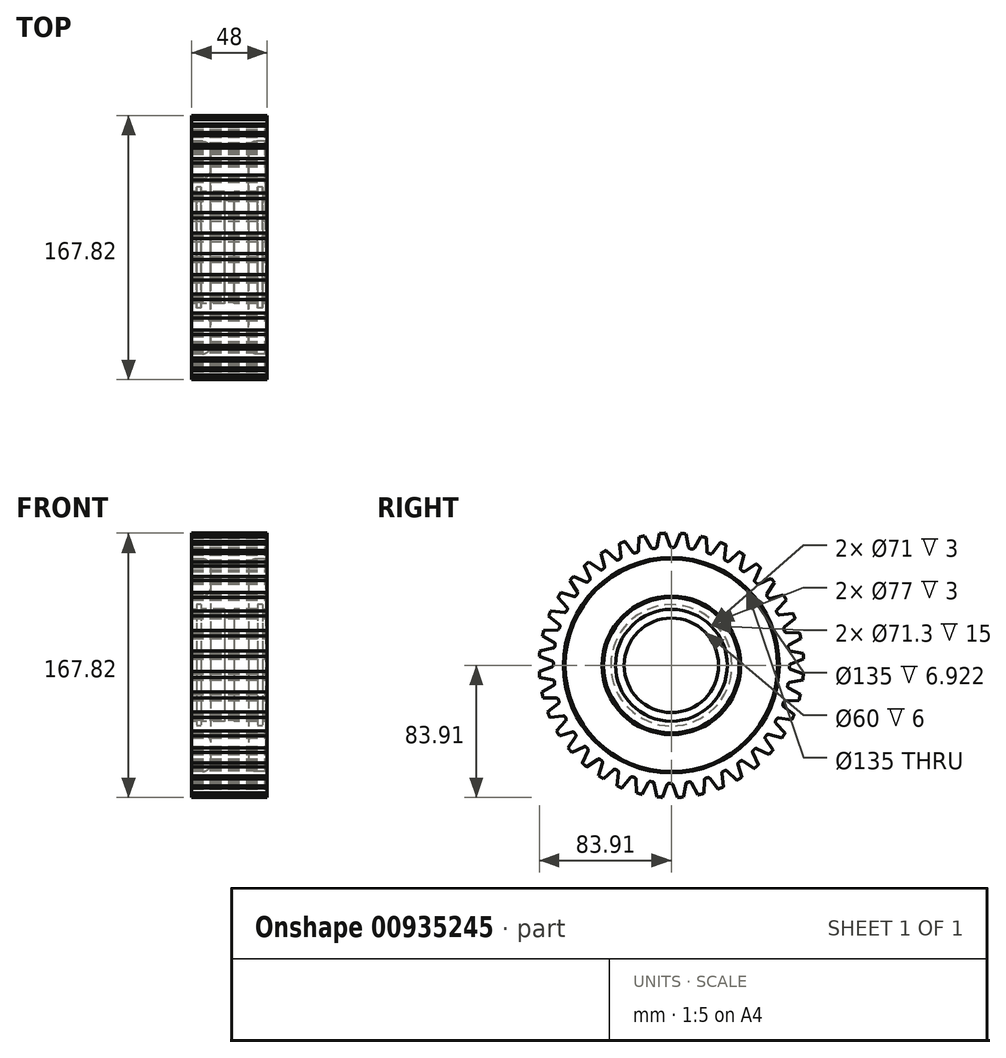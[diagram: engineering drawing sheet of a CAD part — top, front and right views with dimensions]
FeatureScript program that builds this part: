
annotation { "Feature Type Name" : "Feature", "Feature Type Description" : "" }
export const myFeature = defineFeature(function(context is Context, id is Id, definition is map)
    precondition{}
    {
        {
            var Q0;
            Q0=qCreatedBy(makeId("Front.planeOp"),FACE);
            var sketch = newSketch(context, id + "F0", { "sketchPlane" : qUnion([Q0])});
            skLineSegment(sketch, "E0", {"start": v(0, 84) * mm, "end": v(-24, 84) * mm});
            skLineSegment(sketch, "E1", {"start": v(-24, 84) * mm, "end": v(-24, 67.5) * mm});
            skLineSegment(sketch, "E2", {"start": v(-24, 0) * mm, "end": v(0, 0) * mm});
            skLineSegment(sketch, "E3", {"start": v(-24, 35.5) * mm, "end": v(-21, 35.5) * mm});
            skLineSegment(sketch, "E4", {"start": v(-21, 35.5) * mm, "end": v(-21, 38.5) * mm});
            skLineSegment(sketch, "E5", {"start": v(-21, 38.5) * mm, "end": v(-18, 38.5) * mm});
            skLineSegment(sketch, "E6", {"start": v(-18, 38.5) * mm, "end": v(-18, 35.65) * mm});
            skLineSegment(sketch, "E7", {"start": v(-18, 35.65) * mm, "end": v(-3, 35.65) * mm});
            skLineSegment(sketch, "E8", {"start": v(-3, 35.65) * mm, "end": v(-3, 30) * mm});
            skLineSegment(sketch, "E9", {"start": v(-3, 30) * mm, "end": v(0, 30) * mm});
            skLineSegment(sketch, "E10", {"start": v(-24, 44) * mm, "end": v(-17.08, 44) * mm});
            skLineSegment(sketch, "E11", {"start": v(-12, 49.08) * mm, "end": v(-12, 62.42) * mm});
            skLineSegment(sketch, "E12", {"start": v(-17.08, 67.5) * mm, "end": v(-24, 67.5) * mm});
            skPoint(sketch, "E13.visualSharp", {"position": v(-12, 67.5) * mm});
            skArc(sketch, "E13.filletArc", {"start": v(-12, 62.42) * mm, "mid": v(-13.49, 66.01) * mm, "end": v(-17.08, 67.5) * mm});
            skPoint(sketch, "E14.visualSharp", {"position": v(-12, 44) * mm});
            skArc(sketch, "E14.filletArc", {"start": v(-17.08, 44) * mm, "mid": v(-13.49, 45.49) * mm, "end": v(-12, 49.08) * mm});
            skLineSegment(sketch, "E15.trimOffspring", {"start": v(-24, 44) * mm, "end": v(-24, 35.5) * mm});
            skLineSegment(sketch, "E16.MirrorCS", {"start": v(0, 84) * mm, "end": v(24, 84) * mm});
            skLineSegment(sketch, "E17.MirrorCS", {"start": v(24, 84) * mm, "end": v(24, 67.5) * mm});
            skLineSegment(sketch, "E18.MirrorCS", {"start": v(17.08, 67.5) * mm, "end": v(24, 67.5) * mm});
            skArc(sketch, "E19.MirrorCS", {"start": v(12, 62.42) * mm, "mid": v(13.49, 66.01) * mm, "end": v(17.08, 67.5) * mm});
            skLineSegment(sketch, "E20.MirrorCS", {"start": v(12, 49.08) * mm, "end": v(12, 62.42) * mm});
            skArc(sketch, "E21.MirrorCS", {"start": v(17.08, 44) * mm, "mid": v(13.49, 45.49) * mm, "end": v(12, 49.08) * mm});
            skLineSegment(sketch, "E22.MirrorCS", {"start": v(24, 44) * mm, "end": v(17.08, 44) * mm});
            skLineSegment(sketch, "E23.MirrorCS", {"start": v(24, 44) * mm, "end": v(24, 35.5) * mm});
            skLineSegment(sketch, "E24.MirrorCS", {"start": v(24, 35.5) * mm, "end": v(21, 35.5) * mm});
            skLineSegment(sketch, "E25.MirrorCS", {"start": v(21, 38.5) * mm, "end": v(18, 38.5) * mm});
            skLineSegment(sketch, "E26.MirrorCS", {"start": v(21, 35.5) * mm, "end": v(21, 38.5) * mm});
            skLineSegment(sketch, "E27.MirrorCS", {"start": v(18, 38.5) * mm, "end": v(18, 35.65) * mm});
            skLineSegment(sketch, "E28.MirrorCS", {"start": v(18, 35.65) * mm, "end": v(3, 35.65) * mm});
            skLineSegment(sketch, "E29.MirrorCS", {"start": v(3, 35.65) * mm, "end": v(3, 30) * mm});
            skLineSegment(sketch, "E30.MirrorCS", {"start": v(3, 30) * mm, "end": v(0, 30) * mm});
            skSolve(sketch);
        }
        {
            var Q0;
            Q0=makeQuery(id+"F0.imprint","IMPRINT",FACE,{"disambiguationData":[TD([[makeQuery(id+"F0.imprint","IMPRINT",EDGE,{"derivedFrom":sQuery(id+"F0.wireOp",EDGE,"E0")}),1.0]])]});
            var Q1;
            Q1=sQuery(id+"F0.wireOp",EDGE,"E2");
            revolve(context, id + "F1", {"surfaceOperationType" : NewSurfaceOperationType.NEW, "entities" : qUnion([Q0]), "axis" : qUnion([Q1]), "revolveType" : RevolveType.FULL});
        }
        {
            var Q0;
            Q0=qCreatedBy(makeId("Right.planeOp"),FACE);
            var sketch = newSketch(context, id + "F2", { "sketchPlane" : qUnion([Q0])});
            skArc(sketch, "E31", {"start": v(1.48, 74.99) * mm, "mid": v(0.85, 75) * mm, "end": v(0.23, 75) * mm});
            skArc(sketch, "E32.0.0", {"start": v(5.6, 83.81) * mm, "mid": v(0.85, 84) * mm, "end": v(-3.9, 83.9) * mm});
            skLineSegment(sketch, "E33", {"start": v(2.7, 75.82) * mm, "end": v(5.6, 83.81) * mm});
            skLineSegment(sketch, "E34.MirrorCS", {"start": v(-0.96, 75.84) * mm, "end": v(-3.9, 83.9) * mm});
            skPoint(sketch, "E35.trimOffspring.end.orphan", {"position": v(-0.9, 84.76) * mm});
            skPoint(sketch, "E36.visualSharp", {"position": v(-0.66, 75) * mm});
            skArc(sketch, "E36.filletArc", {"start": v(-0.96, 75.84) * mm, "mid": v(-0.5, 75.23) * mm, "end": v(0.23, 75) * mm});
            skPoint(sketch, "E37.visualSharp", {"position": v(2.38, 74.96) * mm});
            skArc(sketch, "E37.filletArc", {"start": v(1.48, 74.99) * mm, "mid": v(2.22, 75.2) * mm, "end": v(2.7, 75.82) * mm});
            skSolve(sketch);
        }
        {
            var Q0;
            Q0=makeQuery(id+"F2.imprint","IMPRINT",FACE,{"disambiguationData":[TD([[makeQuery(id+"F2.imprint","IMPRINT",EDGE,{"derivedFrom":sQuery(id+"F2.wireOp",EDGE,"E31")}),-1.0]])]});
            extrude(context, id + "F3", {"entities" : qUnion([Q0]), "operationType" : NewBodyOperationType.REMOVE, "oppositeDirection" : true, "depth" : 50.8 * mm, "offsetDistance" : 25.4 * mm, "symmetric" : true});
        }
        {
            var Q0;
            Q0=makeQuery(id+"F3.boolean.opBoolean","COPY",FACE,{"derivedFrom":makeQuery(id+"F3.opExtrude","SWEPT_FACE",FACE,{"disambiguationData":[OSD([sQuery(id+"F2.wireOp",EDGE,"E34.MirrorCS")])]})});
            var Q1;
            Q1=makeQuery(id+"F3.boolean.opBoolean","COPY",FACE,{"derivedFrom":makeQuery(id+"F3.opExtrude","SWEPT_FACE",FACE,{"disambiguationData":[OSD([sQuery(id+"F2.wireOp",EDGE,"E36.filletArc")])]})});
            var Q2;
            Q2=makeQuery(id+"F3.boolean.opBoolean","COPY",FACE,{"derivedFrom":makeQuery(id+"F3.opExtrude","SWEPT_FACE",FACE,{"disambiguationData":[OSD([sQuery(id+"F2.wireOp",EDGE,"E31")])]})});
            var Q3;
            Q3=makeQuery(id+"F3.boolean.opBoolean","COPY",FACE,{"derivedFrom":makeQuery(id+"F3.opExtrude","SWEPT_FACE",FACE,{"disambiguationData":[OSD([sQuery(id+"F2.wireOp",EDGE,"E37.filletArc")])]})});
            var Q4;
            Q4=makeQuery(id+"F3.boolean.opBoolean","COPY",FACE,{"derivedFrom":makeQuery(id+"F3.opExtrude","SWEPT_FACE",FACE,{"disambiguationData":[OSD([sQuery(id+"F2.wireOp",EDGE,"E33")])]})});
            var Q5;
            Q5=makeQuery(id+"F1.opRevolve","SWEPT_FACE",FACE,{"disambiguationData":[OSD([sQuery(id+"F0.wireOp",EDGE,"E0"),sQuery(id+"F0.wireOp",EDGE,"E16.MirrorCS")])]});
            circularPattern(context, id + "F4", {"patternType" : PatternType.FACE, "operationType" : NewBodyOperationType.ADD, "faces" : qUnion([Q0, Q1, Q2, Q3, Q4]), "axis" : qUnion([Q5]), "angle" : 9 * degree, "instanceCount" : 40});
        }
        {
            var Q0;
            Q0=makeQuery(id+"F1.opRevolve","SWEPT_EDGE",EDGE,{"disambiguationData":[OSD([sQuery(id+"F0.wireOp",EDGE,"E17.MirrorCS"),sQuery(id+"F0.wireOp",EDGE,"E18.MirrorCS")])]});
            var Q1;
            Q1=makeQuery(id+"F1.opRevolve","SWEPT_EDGE",EDGE,{"disambiguationData":[OSD([sQuery(id+"F0.wireOp",EDGE,"E22.MirrorCS"),sQuery(id+"F0.wireOp",EDGE,"E23.MirrorCS")])]});
            chamfer(context, id + "F5", {"entities" : qUnion([Q0, Q1]), "chamferType" : ChamferType.OFFSET_ANGLE, "width" : 1 * mm, "oppositeDirection" : false, "angle" : 45 * degree, "tangentPropagation" : true});
        }
    });
